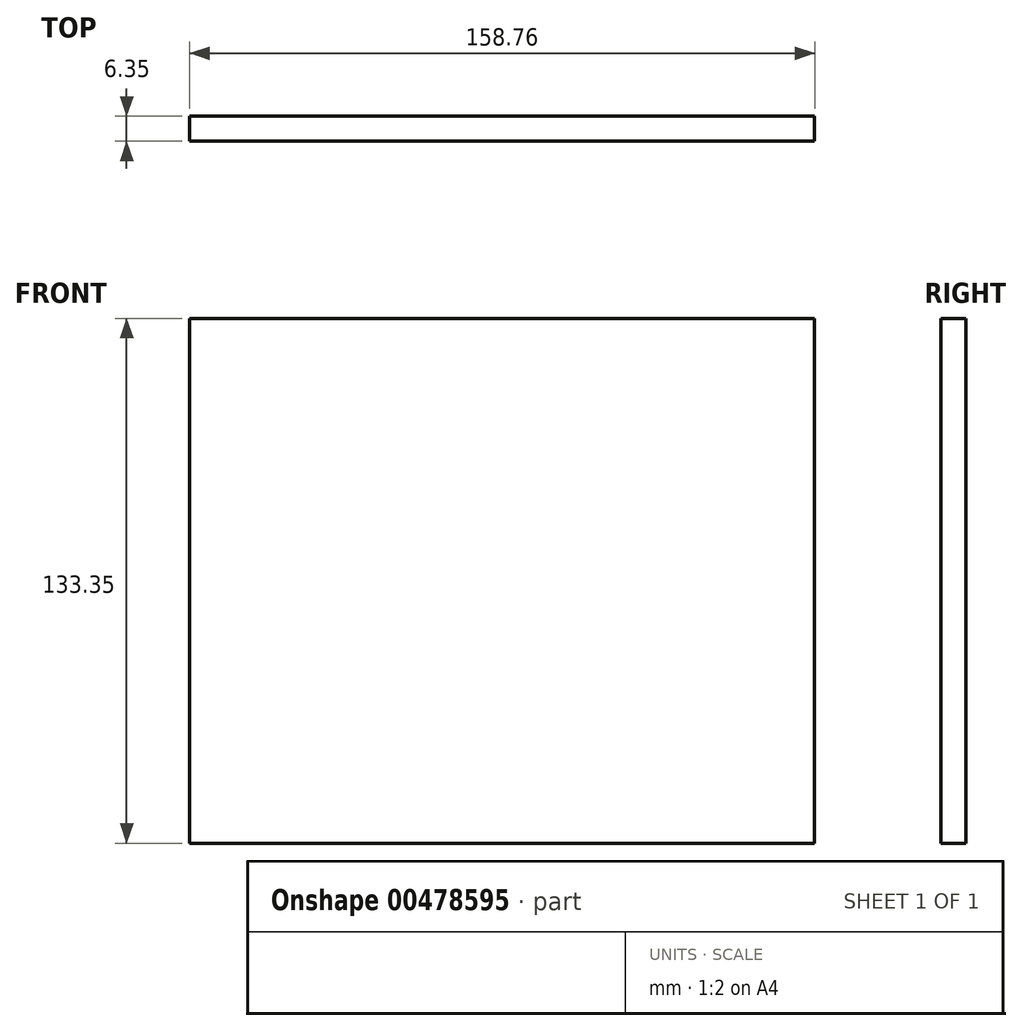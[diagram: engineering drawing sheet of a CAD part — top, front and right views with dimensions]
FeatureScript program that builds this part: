
annotation { "Feature Type Name" : "Feature", "Feature Type Description" : "" }
export const myFeature = defineFeature(function(context is Context, id is Id, definition is map)
    precondition{}
    {
        {
            var Q0;
            Q0=qCreatedBy(makeId("Top.planeOp"),FACE);
            var sketch = newSketch(context, id + "F0", { "sketchPlane" : qUnion([Q0])});
            skLineSegment(sketch, "E0.bottom", {"start": v(-79.38, 0) * mm, "end": v(79.38, 0) * mm});
            skLineSegment(sketch, "E0.top", {"start": v(-79.38, -6.35) * mm, "end": v(79.38, -6.35) * mm});
            skLineSegment(sketch, "E0.left", {"start": v(-79.38, 0) * mm, "end": v(-79.38, -6.35) * mm});
            skLineSegment(sketch, "E0.right", {"start": v(79.38, 0) * mm, "end": v(79.38, -6.35) * mm});
            skSolve(sketch);
        }
        {
            var Q0;
            Q0 = qSketchRegion(id + "F0", true);
            extrude(context, id + "F1", {"entities" : qUnion([Q0]), "depth" : 133.35 * mm});
        }
    });
